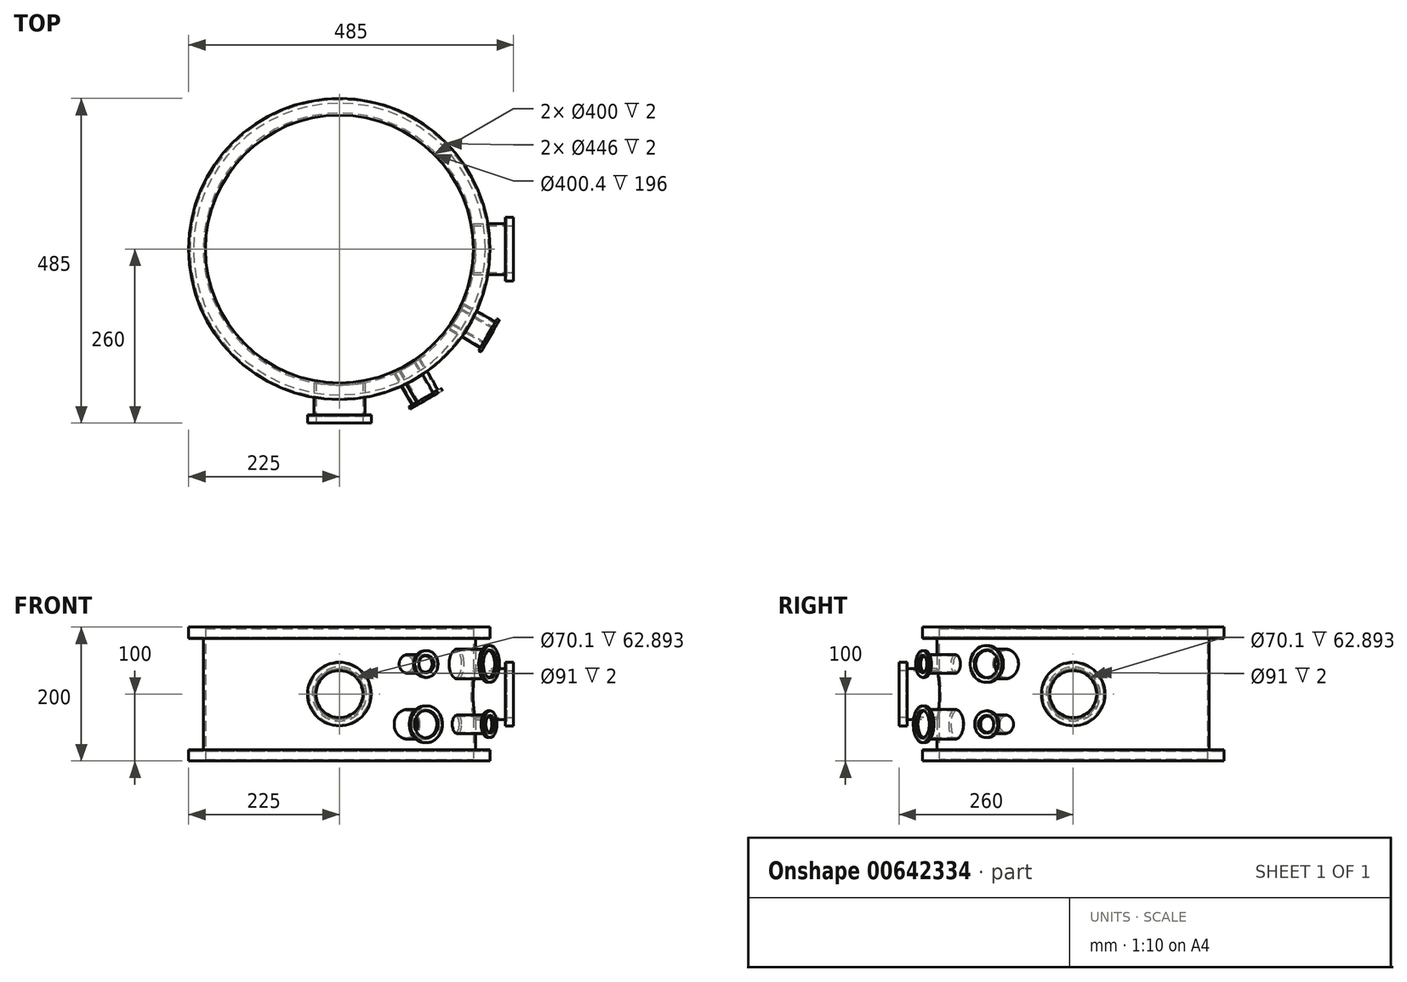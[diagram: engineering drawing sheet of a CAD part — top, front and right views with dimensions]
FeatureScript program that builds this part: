
annotation { "Feature Type Name" : "Feature", "Feature Type Description" : "" }
export const myFeature = defineFeature(function(context is Context, id is Id, definition is map)
    precondition{}
    {
        {
            var Q0;
            Q0=qCreatedBy(makeId("Front.planeOp"),FACE);
            var sketch = newSketch(context, id + "F0", { "sketchPlane" : qUnion([Q0])});
            skLineSegment(sketch, "E0", {"start": v(200, 0) * mm, "end": v(200, 2) * mm});
            skLineSegment(sketch, "E1", {"start": v(200.2, 2) * mm, "end": v(200, 2) * mm});
            skLineSegment(sketch, "E2", {"start": v(200.2, 2) * mm, "end": v(200.2, 198) * mm});
            skLineSegment(sketch, "E3", {"start": v(200, 198) * mm, "end": v(200.2, 198) * mm});
            skLineSegment(sketch, "E4", {"start": v(200, 198) * mm, "end": v(200, 200) * mm});
            skLineSegment(sketch, "E5", {"start": v(200, 200) * mm, "end": v(211, 200) * mm});
            skLineSegment(sketch, "E6", {"start": v(225, 200) * mm, "end": v(225, 183) * mm});
            skLineSegment(sketch, "E7", {"start": v(225, 183) * mm, "end": v(223, 183) * mm});
            skLineSegment(sketch, "E8", {"start": v(203.2, 183) * mm, "end": v(203.2, 17) * mm});
            skLineSegment(sketch, "E9", {"start": v(203.2, 17) * mm, "end": v(218, 17) * mm});
            skLineSegment(sketch, "E10", {"start": v(225, 17) * mm, "end": v(225, 0) * mm});
            skLineSegment(sketch, "E11.trimOffspring", {"start": v(207.48, 200) * mm, "end": v(225, 200) * mm});
            skLineSegment(sketch, "E12", {"start": v(223, 17) * mm, "end": v(223, 15) * mm});
            skLineSegment(sketch, "E13", {"start": v(223, 15) * mm, "end": v(218, 15) * mm});
            skLineSegment(sketch, "E14", {"start": v(218, 15) * mm, "end": v(218, 17) * mm});
            skLineSegment(sketch, "E15.trimOffspring", {"start": v(223, 17) * mm, "end": v(225, 17) * mm});
            skLineSegment(sketch, "E16", {"start": v(218, 183) * mm, "end": v(218, 185) * mm});
            skLineSegment(sketch, "E17", {"start": v(218, 185) * mm, "end": v(223, 185) * mm});
            skLineSegment(sketch, "E18", {"start": v(223, 185) * mm, "end": v(223, 183) * mm});
            skLineSegment(sketch, "E19.trimOffspring", {"start": v(218, 183) * mm, "end": v(203.2, 183) * mm});
            skLineSegment(sketch, "E20", {"start": v(200, 0) * mm, "end": v(225, 0) * mm});
            skSolve(sketch);
        }
        {
            var Q0;
            Q0=qCreatedBy(makeId("Front.planeOp"),FACE);
            var sketch = newSketch(context, id + "F1", { "sketchPlane" : qUnion([Q0])});
            skLineSegment(sketch, "E21", {"start": v(0, 0) * mm, "end": v(0, 128.06) * mm, "construction": true});
            skSolve(sketch);
        }
        {
            var Q0;
            Q0=makeQuery(id+"F0.imprint","IMPRINT",FACE,{"disambiguationData":[TD([[makeQuery(id+"F0.imprint","IMPRINT",EDGE,{"derivedFrom":sQuery(id+"F0.wireOp",EDGE,"E0")}),-1.0]])]});
            var Q1;
            Q1=sQuery(id+"F1.wireOp",EDGE,"E21");
            revolve(context, id + "F2", {"entities" : qUnion([Q0]), "axis" : qUnion([Q1]), "revolveType" : RevolveType.FULL});
        }
        {
            var Q0;
            Q0=qCreatedBy(makeId("Right.planeOp"),FACE);
            cPlane(context, id + "F3", {"entities" : qUnion([Q0]), "cplaneType" : CPlaneType.OFFSET, "offset" : 248 * mm, "width" : 150 * mm, "height" : 150 * mm});
        }
        {
            var Q0;
            Q0=qCreatedBy(id+"F3.planeOp",FACE);
            var sketch = newSketch(context, id + "F4", { "sketchPlane" : qUnion([Q0])});
            skCircle(sketch, "E22", {"center": v(0, 100) * mm, "radius": 38.05 * mm});
            skLineSegment(sketch, "E23", {"start": v(0, 100) * mm, "end": v(0, 0) * mm, "construction": true});
            skLineSegment(sketch, "E24", {"start": v(0, 100) * mm, "end": v(0, 200) * mm, "construction": true});
            skCircle(sketch, "E25.0", {"center": v(0, 100) * mm, "radius": 35.05 * mm});
            skSolve(sketch);
        }
        {
            var Q0;
            Q0=makeQuery(id+"F4.imprint","IMPRINT",FACE,{"disambiguationData":[TD([[makeQuery(id+"F4.imprint","IMPRINT",EDGE,{"derivedFrom":sQuery(id+"F4.wireOp",EDGE,"E22")}),1.0]])]});
            var Q1;
            Q1=makeQuery(id+"F2.opRevolve","SWEPT_FACE",FACE,{"disambiguationData":[OSD([sQuery(id+"F0.wireOp",EDGE,"E8")])]});
            extrude(context, id + "F5", {"entities" : qUnion([Q0]), "operationType" : NewBodyOperationType.ADD, "endBound" : BoundingType.UP_TO_SURFACE, "oppositeDirection" : true, "depth" : 25 * mm, "endBoundEntityFace" : qUnion([Q1]), "offsetDistance" : 25 * mm});
        }
        {
            var Q0;
            Q0=makeQuery(id+"F4.imprint","IMPRINT",FACE,{"disambiguationData":[TD([[makeQuery(id+"F4.imprint","IMPRINT",EDGE,{"derivedFrom":sQuery(id+"F4.wireOp",EDGE,"E25.0")}),1.0]])]});
            extrude(context, id + "F6", {"entities" : qUnion([Q0]), "operationType" : NewBodyOperationType.REMOVE, "oppositeDirection" : true, "depth" : 100 * mm, "offsetDistance" : 25 * mm});
        }
        {
            var Q0;
            Q0=makeQuery(id+"F5.opExtrude","CAP_FACE",FACE,{"disambiguationData":[OSD([sQuery(id+"F4.wireOp",EDGE,"E22"),sQuery(id+"F4.wireOp",EDGE,"E25.0")])],"isStart":true});
            var sketch = newSketch(context, id + "F7", { "sketchPlane" : qUnion([Q0])});
            skCircle(sketch, "E26", {"center": v(0, 100) * mm, "radius": 47.5 * mm});
            skCircle(sketch, "E27", {"center": v(0, 100) * mm, "radius": 35 * mm});
            skSolve(sketch);
        }
        {
            var Q0;
            Q0=makeQuery(id+"F7.imprint","IMPRINT",FACE,{"disambiguationData":[TD([[makeQuery(id+"F7.imprint","IMPRINT",EDGE,{"derivedFrom":sQuery(id+"F7.wireOp",EDGE,"E26")}),1.0]])]});
            var Q1;
            Q1=makeQuery(id+"F7.imprint","IMPRINT",FACE,{"disambiguationData":[TD([[makeQuery(id+"F7.imprint","IMPRINT",EDGE,{"derivedFrom":makeQuery(id+"F5.opExtrude","CAP_EDGE",EDGE,{"disambiguationData":[OSD([sQuery(id+"F4.wireOp",EDGE,"E22")])],"isStart":true})}),1.0]])]});
            extrude(context, id + "F8", {"entities" : qUnion([Q0, Q1]), "operationType" : NewBodyOperationType.ADD, "depth" : 12 * mm, "offsetDistance" : 25 * mm});
        }
        {
            var Q0;
            Q0=makeQuery(id+"F8.opExtrude","CAP_FACE",FACE,{"disambiguationData":[OSD([sQuery(id+"F4.wireOp",EDGE,"E25.0"),sQuery(id+"F7.wireOp",EDGE,"E26")])],"isStart":true});
            var sketch = newSketch(context, id + "F9", { "sketchPlane" : qUnion([Q0])});
            skCircle(sketch, "E28", {"center": v(0, 100) * mm, "radius": 45.5 * mm});
            skCircle(sketch, "E29", {"center": v(0, 100) * mm, "radius": 40.5 * mm});
            skSolve(sketch);
        }
        {
            var Q0;
            Q0=makeQuery(id+"F9.imprint","IMPRINT",FACE,{"disambiguationData":[TD([[makeQuery(id+"F9.imprint","IMPRINT",EDGE,{"derivedFrom":sQuery(id+"F9.wireOp",EDGE,"E28")}),1.0]])]});
            extrude(context, id + "F10", {"entities" : qUnion([Q0]), "operationType" : NewBodyOperationType.REMOVE, "oppositeDirection" : true, "depth" : 2 * mm, "offsetDistance" : 25 * mm});
        }
        {
            var Q0;
            Q0=qCreatedBy(makeId("Front.planeOp"),FACE);
            cPlane(context, id + "F11", {"entities" : qUnion([Q0]), "cplaneType" : CPlaneType.OFFSET, "offset" : 248 * mm, "width" : 150 * mm, "height" : 150 * mm});
        }
        {
            var Q0;
            Q0=qCreatedBy(id+"F11.planeOp",FACE);
            var sketch = newSketch(context, id + "F12", { "sketchPlane" : qUnion([Q0])});
            skCircle(sketch, "E30", {"center": v(0, 100) * mm, "radius": 38.05 * mm});
            skLineSegment(sketch, "E31", {"start": v(0, 100) * mm, "end": v(0, 0) * mm, "construction": true});
            skLineSegment(sketch, "E32", {"start": v(0, 100) * mm, "end": v(0, 200) * mm, "construction": true});
            skCircle(sketch, "E33.0", {"center": v(0, 100) * mm, "radius": 35.05 * mm});
            skSolve(sketch);
        }
        {
            var Q0;
            Q0=makeQuery(id+"F12.imprint","IMPRINT",FACE,{"disambiguationData":[TD([[makeQuery(id+"F12.imprint","IMPRINT",EDGE,{"derivedFrom":sQuery(id+"F12.wireOp",EDGE,"E33.0")}),1.0]])]});
            extrude(context, id + "F13", {"entities" : qUnion([Q0]), "operationType" : NewBodyOperationType.REMOVE, "oppositeDirection" : true, "depth" : 100 * mm, "offsetDistance" : 25 * mm});
        }
        {
            var Q0;
            Q0=makeQuery(id+"F12.imprint","IMPRINT",FACE,{"disambiguationData":[TD([[makeQuery(id+"F12.imprint","IMPRINT",EDGE,{"derivedFrom":sQuery(id+"F12.wireOp",EDGE,"E30")}),1.0]])]});
            extrude(context, id + "F14", {"entities" : qUnion([Q0]), "operationType" : NewBodyOperationType.ADD, "endBound" : BoundingType.UP_TO_NEXT, "oppositeDirection" : true, "depth" : 25 * mm, "offsetDistance" : 25 * mm});
        }
        {
            var Q0;
            Q0=makeQuery(id+"F14.opExtrude","CAP_FACE",FACE,{"disambiguationData":[OSD([sQuery(id+"F12.wireOp",EDGE,"E30"),sQuery(id+"F12.wireOp",EDGE,"E33.0")])],"isStart":true});
            var sketch = newSketch(context, id + "F15", { "sketchPlane" : qUnion([Q0])});
            skCircle(sketch, "E34", {"center": v(0, 100) * mm, "radius": 35 * mm});
            skCircle(sketch, "E35", {"center": v(0, 100) * mm, "radius": 47.5 * mm});
            skSolve(sketch);
        }
        {
            var Q0;
            Q0=makeQuery(id+"F15.imprint","IMPRINT",FACE,{"disambiguationData":[TD([[makeQuery(id+"F15.imprint","IMPRINT",EDGE,{"derivedFrom":makeQuery(id+"F14.opExtrude","CAP_EDGE",EDGE,{"disambiguationData":[OSD([sQuery(id+"F12.wireOp",EDGE,"E30")])],"isStart":true})}),1.0]])]});
            var Q1;
            Q1=makeQuery(id+"F15.imprint","IMPRINT",FACE,{"disambiguationData":[TD([[makeQuery(id+"F15.imprint","IMPRINT",EDGE,{"derivedFrom":sQuery(id+"F15.wireOp",EDGE,"E35")}),1.0]])]});
            extrude(context, id + "F16", {"entities" : qUnion([Q0, Q1]), "operationType" : NewBodyOperationType.ADD, "depth" : 12 * mm, "offsetDistance" : 25 * mm});
        }
        {
            var Q0;
            Q0=makeQuery(id+"F16.opExtrude","CAP_FACE",FACE,{"disambiguationData":[OSD([sQuery(id+"F12.wireOp",EDGE,"E33.0"),sQuery(id+"F15.wireOp",EDGE,"E35")])],"isStart":true});
            var sketch = newSketch(context, id + "F17", { "sketchPlane" : qUnion([Q0])});
            skCircle(sketch, "E36", {"center": v(0, 100) * mm, "radius": 40.5 * mm});
            skCircle(sketch, "E37", {"center": v(0, 100) * mm, "radius": 45.5 * mm});
            skSolve(sketch);
        }
        {
            var Q0;
            Q0=makeQuery(id+"F17.imprint","IMPRINT",FACE,{"disambiguationData":[TD([[makeQuery(id+"F17.imprint","IMPRINT",EDGE,{"derivedFrom":sQuery(id+"F17.wireOp",EDGE,"E36")}),-1.0]])]});
            extrude(context, id + "F18", {"entities" : qUnion([Q0]), "operationType" : NewBodyOperationType.REMOVE, "oppositeDirection" : true, "depth" : 2 * mm, "offsetDistance" : 25 * mm});
        }
        {
            var Q0;
            Q0=qCreatedBy(makeId("Top.planeOp"),FACE);
            var sketch = newSketch(context, id + "F19", { "sketchPlane" : qUnion([Q0])});
            skLineSegment(sketch, "E38", {"start": v(0, 0) * mm, "end": v(128, -221.7) * mm, "construction": true});
            skLineSegment(sketch, "E39", {"start": v(0, 0) * mm, "end": v(221.7, -128) * mm, "construction": true});
            skSolve(sketch);
        }
        {
            var Q0;
            Q0=sQuery(id+"F19.wireOp",EDGE,"E38");
            var Q1;
            Q1=sQuery(id+"F19.wireOp",VERTEX,"E38.end");
            cPlane(context, id + "F20", {"entities" : qUnion([Q0, Q1]), "cplaneType" : CPlaneType.LINE_POINT, "offset" : 25 * mm, "width" : 150 * mm, "height" : 150 * mm});
        }
        {
            var Q0;
            Q0=qCreatedBy(id+"F20.planeOp",FACE);
            var sketch = newSketch(context, id + "F21", { "sketchPlane" : qUnion([Q0])});
            skCircle(sketch, "E40", {"center": v(0, 145) * mm, "radius": 14 * mm});
            skCircle(sketch, "E41", {"center": v(0, 55) * mm, "radius": 22.25 * mm});
            skLineSegment(sketch, "E42", {"start": v(0, 145) * mm, "end": v(0, 55) * mm, "construction": true});
            skLineSegment(sketch, "E43", {"start": v(0, 55) * mm, "end": v(0, 0) * mm, "construction": true});
            skLineSegment(sketch, "E44", {"start": v(0, 145) * mm, "end": v(0, 200) * mm, "construction": true});
            skCircle(sketch, "E45.0", {"center": v(0, 145) * mm, "radius": 12 * mm});
            skCircle(sketch, "E46", {"center": v(0, 55) * mm, "radius": 20.25 * mm});
            skSolve(sketch);
        }
        {
            var Q0;
            Q0=makeQuery(id+"F21.imprint","IMPRINT",FACE,{"disambiguationData":[TD([[makeQuery(id+"F21.imprint","IMPRINT",EDGE,{"derivedFrom":sQuery(id+"F21.wireOp",EDGE,"E45.0")}),1.0]])]});
            var Q1;
            Q1=makeQuery(id+"F21.imprint","IMPRINT",FACE,{"disambiguationData":[TD([[makeQuery(id+"F21.imprint","IMPRINT",EDGE,{"derivedFrom":sQuery(id+"F21.wireOp",EDGE,"E46")}),1.0]])]});
            extrude(context, id + "F22", {"entities" : qUnion([Q0, Q1]), "operationType" : NewBodyOperationType.REMOVE, "oppositeDirection" : true, "depth" : 100 * mm, "offsetDistance" : 25 * mm});
        }
        {
            var Q0;
            Q0=makeQuery(id+"F21.imprint","IMPRINT",FACE,{"disambiguationData":[TD([[makeQuery(id+"F21.imprint","IMPRINT",EDGE,{"derivedFrom":sQuery(id+"F21.wireOp",EDGE,"E40")}),1.0]])]});
            var Q1;
            Q1=makeQuery(id+"F21.imprint","IMPRINT",FACE,{"disambiguationData":[TD([[makeQuery(id+"F21.imprint","IMPRINT",EDGE,{"derivedFrom":sQuery(id+"F21.wireOp",EDGE,"E41")}),1.0]])]});
            extrude(context, id + "F23", {"entities" : qUnion([Q0, Q1]), "operationType" : NewBodyOperationType.ADD, "endBound" : BoundingType.UP_TO_NEXT, "oppositeDirection" : true, "depth" : 25 * mm, "offsetDistance" : 25 * mm});
        }
        {
            var Q0;
            Q0=makeQuery(id+"F21.imprint","IMPRINT",FACE,{"disambiguationData":[TD([[makeQuery(id+"F21.imprint","IMPRINT",EDGE,{"derivedFrom":sQuery(id+"F21.wireOp",EDGE,"E41")}),1.0]])]});
            var sketch = newSketch(context, id + "F24", { "sketchPlane" : qUnion([Q0])});
            skCircle(sketch, "E47", {"center": v(0, 55) * mm, "radius": 20.5 * mm});
            skCircle(sketch, "E48", {"center": v(0, 55) * mm, "radius": 27.5 * mm});
            skCircle(sketch, "E49", {"center": v(0, 145) * mm, "radius": 13 * mm});
            skCircle(sketch, "E50", {"center": v(0, 145) * mm, "radius": 20 * mm});
            skCircle(sketch, "E51", {"center": v(0, 145) * mm, "radius": 36 * mm, "construction": true});
            skCircle(sketch, "E52", {"center": v(0, 55) * mm, "radius": 45 * mm, "construction": true});
            skSolve(sketch);
        }
        {
            var Q0;
            Q0=makeQuery(id+"F24.imprint","IMPRINT",FACE,{"disambiguationData":[TD([[makeQuery(id+"F24.imprint","IMPRINT",EDGE,{"derivedFrom":sQuery(id+"F24.wireOp",EDGE,"E49")}),-1.0]])]});
            var Q1;
            Q1=makeQuery(id+"F24.imprint","IMPRINT",FACE,{"disambiguationData":[TD([[makeQuery(id+"F24.imprint","IMPRINT",EDGE,{"derivedFrom":sQuery(id+"F24.wireOp",EDGE,"E47")}),-1.0]])]});
            var Q2;
            Q2=makeQuery(id+"F24.imprint","IMPRINT",FACE,{"disambiguationData":[TD([[makeQuery(id+"F24.imprint","IMPRINT",EDGE,{"derivedFrom":sQuery(id+"F24.wireOp",EDGE,"E48")}),1.0]])]});
            extrude(context, id + "F25", {"entities" : qUnion([Q0, Q1, Q2]), "operationType" : NewBodyOperationType.ADD, "depth" : 4 * mm, "offsetDistance" : 25 * mm});
        }
        {
            var Q0;
            Q0=sQuery(id+"F19.wireOp",EDGE,"E39");
            var Q1;
            Q1=sQuery(id+"F19.wireOp",VERTEX,"E39.end");
            cPlane(context, id + "F26", {"entities" : qUnion([Q0, Q1]), "cplaneType" : CPlaneType.LINE_POINT, "offset" : 25 * mm, "width" : 150 * mm, "height" : 150 * mm});
        }
        {
            var Q0;
            Q0=qCreatedBy(id+"F26.planeOp",FACE);
            var sketch = newSketch(context, id + "F27", { "sketchPlane" : qUnion([Q0])});
            skCircle(sketch, "E53", {"center": v(0, 55) * mm, "radius": 14 * mm});
            skCircle(sketch, "E54", {"center": v(0, 145) * mm, "radius": 22.25 * mm});
            skLineSegment(sketch, "E55", {"start": v(0, 0) * mm, "end": v(0, 55) * mm, "construction": true});
            skLineSegment(sketch, "E56", {"start": v(0, 55) * mm, "end": v(0, 145) * mm, "construction": true});
            skLineSegment(sketch, "E57", {"start": v(0, 145) * mm, "end": v(0, 200) * mm, "construction": true});
            skCircle(sketch, "E58", {"center": v(0, 145) * mm, "radius": 20.25 * mm});
            skCircle(sketch, "E59", {"center": v(0, 55) * mm, "radius": 12 * mm});
            skSolve(sketch);
        }
        {
            var Q0;
            Q0=makeQuery(id+"F27.imprint","IMPRINT",FACE,{"disambiguationData":[TD([[makeQuery(id+"F27.imprint","IMPRINT",EDGE,{"derivedFrom":sQuery(id+"F27.wireOp",EDGE,"E58")}),1.0]])]});
            var Q1;
            Q1=makeQuery(id+"F27.imprint","IMPRINT",FACE,{"disambiguationData":[TD([[makeQuery(id+"F27.imprint","IMPRINT",EDGE,{"derivedFrom":sQuery(id+"F27.wireOp",EDGE,"E59")}),1.0]])]});
            extrude(context, id + "F28", {"entities" : qUnion([Q0, Q1]), "operationType" : NewBodyOperationType.REMOVE, "oppositeDirection" : true, "depth" : 100 * mm, "offsetDistance" : 25 * mm});
        }
        {
            var Q0;
            Q0=makeQuery(id+"F27.imprint","IMPRINT",FACE,{"disambiguationData":[TD([[makeQuery(id+"F27.imprint","IMPRINT",EDGE,{"derivedFrom":sQuery(id+"F27.wireOp",EDGE,"E54")}),1.0]])]});
            var Q1;
            Q1=makeQuery(id+"F27.imprint","IMPRINT",FACE,{"disambiguationData":[TD([[makeQuery(id+"F27.imprint","IMPRINT",EDGE,{"derivedFrom":sQuery(id+"F27.wireOp",EDGE,"E53")}),1.0]])]});
            extrude(context, id + "F29", {"entities" : qUnion([Q0, Q1]), "operationType" : NewBodyOperationType.ADD, "endBound" : BoundingType.UP_TO_NEXT, "oppositeDirection" : true, "depth" : 25 * mm, "offsetDistance" : 25 * mm});
        }
        {
            var Q0;
            Q0=makeQuery(id+"F27.imprint","IMPRINT",FACE,{"disambiguationData":[TD([[makeQuery(id+"F27.imprint","IMPRINT",EDGE,{"derivedFrom":sQuery(id+"F27.wireOp",EDGE,"E54")}),1.0]])]});
            var sketch = newSketch(context, id + "F30", { "sketchPlane" : qUnion([Q0])});
            skCircle(sketch, "E60", {"center": v(0, 145) * mm, "radius": 20.5 * mm});
            skCircle(sketch, "E61", {"center": v(0, 145) * mm, "radius": 27.5 * mm});
            skCircle(sketch, "E62", {"center": v(0, 55) * mm, "radius": 13 * mm});
            skCircle(sketch, "E63", {"center": v(0, 55) * mm, "radius": 20 * mm});
            skSolve(sketch);
        }
        {
            var Q0;
            Q0=makeQuery(id+"F30.imprint","IMPRINT",FACE,{"disambiguationData":[TD([[makeQuery(id+"F30.imprint","IMPRINT",EDGE,{"derivedFrom":sQuery(id+"F30.wireOp",EDGE,"E61")}),1.0]])]});
            var Q1;
            Q1=makeQuery(id+"F30.imprint","IMPRINT",FACE,{"disambiguationData":[TD([[makeQuery(id+"F30.imprint","IMPRINT",EDGE,{"derivedFrom":sQuery(id+"F30.wireOp",EDGE,"E62")}),-1.0]])]});
            var Q2;
            Q2=makeQuery(id+"F30.imprint","IMPRINT",FACE,{"disambiguationData":[TD([[makeQuery(id+"F30.imprint","IMPRINT",EDGE,{"derivedFrom":sQuery(id+"F30.wireOp",EDGE,"E60")}),-1.0]])]});
            extrude(context, id + "F31", {"entities" : qUnion([Q0, Q1, Q2]), "operationType" : NewBodyOperationType.ADD, "depth" : 4 * mm, "offsetDistance" : 25 * mm});
        }
    });
